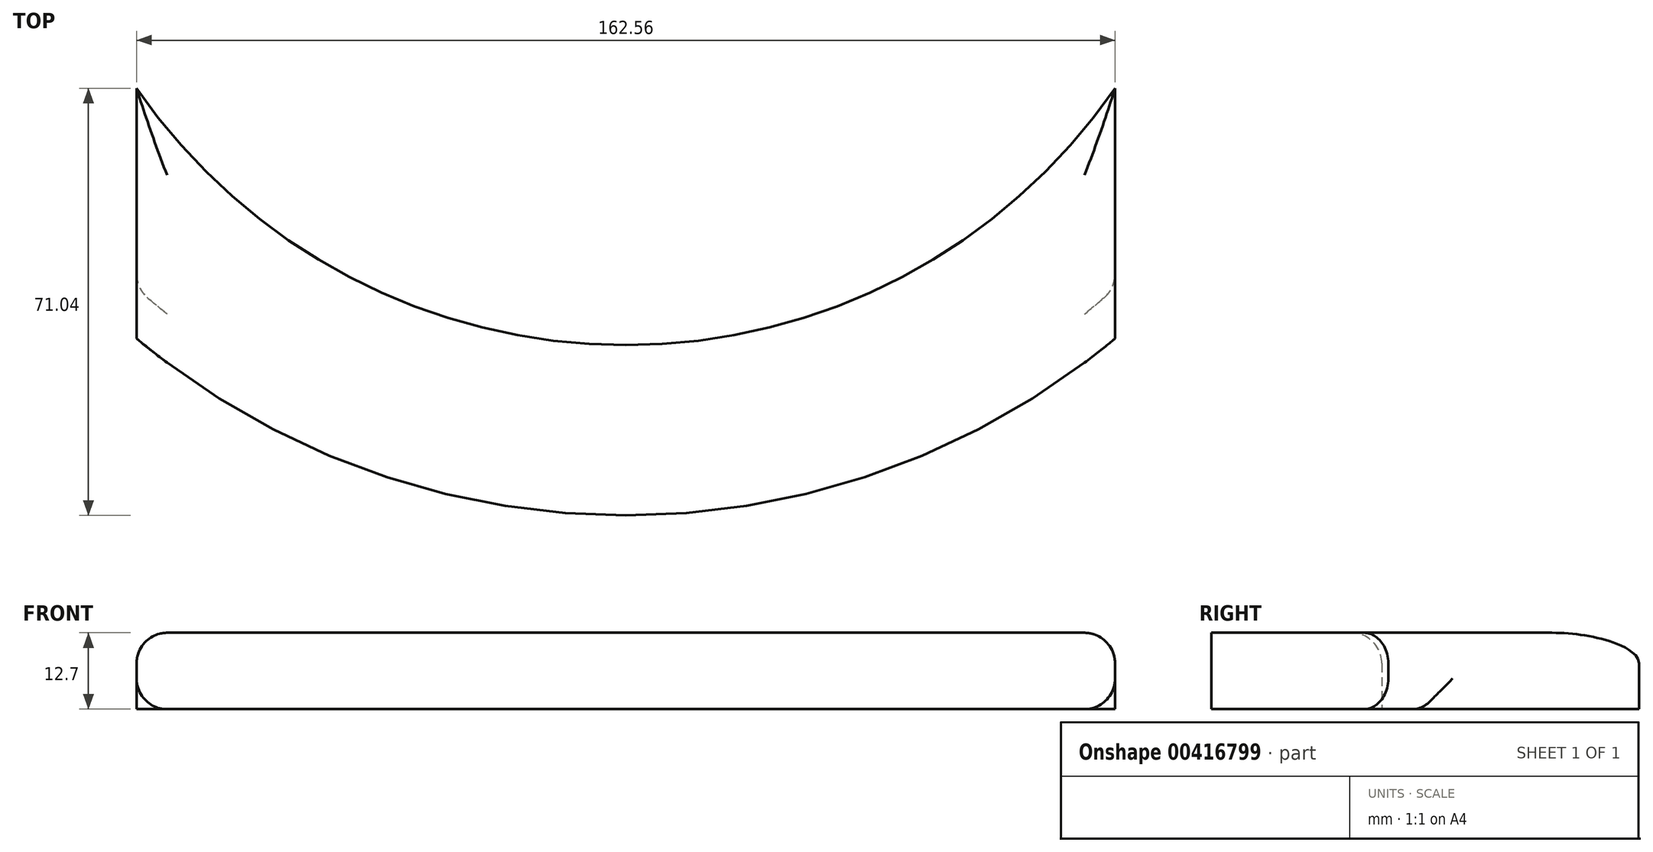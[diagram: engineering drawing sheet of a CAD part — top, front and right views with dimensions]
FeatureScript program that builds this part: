
annotation { "Feature Type Name" : "Feature", "Feature Type Description" : "" }
export const myFeature = defineFeature(function(context is Context, id is Id, definition is map)
    precondition{}
    {
        {
            var Q0;
            Q0=qCreatedBy(makeId("Top.planeOp"),FACE);
            var sketch = newSketch(context, id + "F0", { "sketchPlane" : qUnion([Q0])});
            skArc(sketch, "E0", {"start": v(-81.28, 42.72) * mm, "mid": v(0, 0) * mm, "end": v(81.28, 42.72) * mm});
            skArc(sketch, "E1", {"start": v(-81.28, 1.1) * mm, "mid": v(0, -28.32) * mm, "end": v(81.28, 1.1) * mm});
            skPoint(sketch, "E2.trimOffspring.end.orphan", {"position": v(81.28, 1.1) * mm});
            skLineSegment(sketch, "E3", {"start": v(0, 0) * mm, "end": v(0, -44.65) * mm, "construction": true});
            skLineSegment(sketch, "E4.bottom", {"start": v(-81.28, 42.72) * mm, "end": v(81.28, 42.72) * mm, "construction": true});
            skLineSegment(sketch, "E4.top", {"start": v(-81.28, 1.1) * mm, "end": v(81.28, 1.1) * mm, "construction": true});
            skLineSegment(sketch, "E5", {"start": v(-81.28, 42.72) * mm, "end": v(-81.28, 1.1) * mm, "construction": true});
            skLineSegment(sketch, "E6", {"start": v(81.28, 42.72) * mm, "end": v(81.28, 1.1) * mm, "construction": true});
            skLineSegment(sketch, "E7", {"start": v(-81.28, 42.72) * mm, "end": v(-81.28, 1.1) * mm});
            skLineSegment(sketch, "E8", {"start": v(81.28, 42.72) * mm, "end": v(81.28, 1.1) * mm});
            skSolve(sketch);
        }
        {
            var Q0;
            Q0=qSketchRegion(id+"F0",true);
            extrude(context, id + "F1", {"entities" : qUnion([Q0]), "depth" : 12.7 * mm, "offsetDistance" : 25.4 * mm});
        }
        {
            var Q0;
            Q0=makeQuery(id+"F1.opExtrude","CAP_FACE",FACE,{"disambiguationData":[OSD([sQuery(id+"F0.wireOp",EDGE,"E0"),sQuery(id+"F0.wireOp",EDGE,"E1"),sQuery(id+"F0.wireOp",EDGE,"E7"),sQuery(id+"F0.wireOp",EDGE,"E8")])],"isStart":true});
            var sketch = newSketch(context, id + "F2", { "sketchPlane" : qUnion([Q0])});
            skArc(sketch, "E9.0", {"start": v(-81.28, -9.52) * mm, "mid": v(0, 21.97) * mm, "end": v(81.28, -9.52) * mm});
            skLineSegment(sketch, "E10", {"start": v(81.28, -9.52) * mm, "end": v(81.28, -1.1) * mm});
            skLineSegment(sketch, "E11", {"start": v(-81.28, -9.52) * mm, "end": v(-81.28, -1.1) * mm});
            skArc(sketch, "E12", {"start": v(81.28, -1.1) * mm, "mid": v(0, 28.32) * mm, "end": v(-81.28, -1.1) * mm});
            skSolve(sketch);
        }
        {
            var Q0;
            Q0=makeQuery(id+"F2.imprint","IMPRINT",FACE,{"disambiguationData":[TD([[makeQuery(id+"F2.imprint","IMPRINT",EDGE,{"derivedFrom":sQuery(id+"F2.wireOp",EDGE,"E9.0")}),1.0]])]});
            extrude(context, id + "F3", {"entities" : qUnion([Q0]), "operationType" : NewBodyOperationType.ADD, "depth" : 76.2 * mm, "offsetDistance" : 25.4 * mm});
        }
        {
            var Q0;
            Q0=makeQuery(id+"F1.opExtrude","CAP_EDGE",EDGE,{"disambiguationData":[OSD([sQuery(id+"F0.wireOp",EDGE,"E7")])],"isStart":false});
            var Q1;
            Q1=makeQuery(id+"F1.opExtrude","CAP_EDGE",EDGE,{"disambiguationData":[OSD([sQuery(id+"F0.wireOp",EDGE,"E7")])],"isStart":true});
            var Q2;
            Q2=makeQuery(id+"F3.opExtrude","SWEPT_EDGE",EDGE,{"disambiguationData":[OSD([sQuery(id+"F0.wireOp",EDGE,"E7"),sQuery(id+"F2.wireOp",EDGE,"E9.0"),sQuery(id+"F2.wireOp",EDGE,"E11")])]});
            var Q3;
            Q3=makeQuery(id+"F1.opExtrude","CAP_EDGE",EDGE,{"disambiguationData":[OSD([sQuery(id+"F0.wireOp",EDGE,"E8")])],"isStart":false});
            var Q4;
            Q4=makeQuery(id+"F1.opExtrude","CAP_EDGE",EDGE,{"disambiguationData":[OSD([sQuery(id+"F0.wireOp",EDGE,"E8")])],"isStart":true});
            var Q5;
            Q5=makeQuery(id+"F3.opExtrude","SWEPT_EDGE",EDGE,{"disambiguationData":[OSD([sQuery(id+"F0.wireOp",EDGE,"E8"),sQuery(id+"F2.wireOp",EDGE,"E9.0"),sQuery(id+"F2.wireOp",EDGE,"E10")])]});
            var Q6;
            Q6=makeQuery(id+"F1.opExtrude","CAP_EDGE",EDGE,{"disambiguationData":[OSD([sQuery(id+"F0.wireOp",EDGE,"E0")])],"isStart":false});
            var Q7;
            Q7=makeQuery(id+"F1.opExtrude","CAP_EDGE",EDGE,{"disambiguationData":[OSD([sQuery(id+"F0.wireOp",EDGE,"E0")])],"isStart":true});
            var Q8;
            Q8=makeQuery(id+"F3.opExtrude","CAP_EDGE",EDGE,{"disambiguationData":[OSD([sQuery(id+"F2.wireOp",EDGE,"E9.0")])],"isStart":false});
            fillet(context, id + "F4", {"entities" : qUnion([Q0, Q1, Q2, Q3, Q4, Q5, Q6, Q7, Q8]), "radius" : 5.08 * mm, "tangentPropagation" : true, "allowEdgeOverflow" : false});
        }
        {
            var Q0;
            Q0=qCreatedBy(makeId("Top.planeOp"),FACE);
            var sketch = newSketch(context, id + "F5", { "sketchPlane" : qUnion([Q0])});
            skLineSegment(sketch, "E13.bottom", {"start": v(-101.6, 50.8) * mm, "end": v(101.6, 50.8) * mm});
            skLineSegment(sketch, "E13.top", {"start": v(-101.6, -50.8) * mm, "end": v(101.6, -50.8) * mm});
            skLineSegment(sketch, "E13.left", {"start": v(-101.6, 50.8) * mm, "end": v(-101.6, -50.8) * mm});
            skLineSegment(sketch, "E13.right", {"start": v(101.6, 50.8) * mm, "end": v(101.6, -50.8) * mm});
            skSolve(sketch);
        }
        {
            var Q0;
            Q0 = qSketchRegion(id + "F5", true);
            extrude(context, id + "F6", {"entities" : qUnion([Q0]), "operationType" : NewBodyOperationType.REMOVE, "endBound" : BoundingType.THROUGH_ALL, "oppositeDirection" : true, "depth" : 25.4 * mm, "offsetDistance" : 25.4 * mm});
        }
    });
